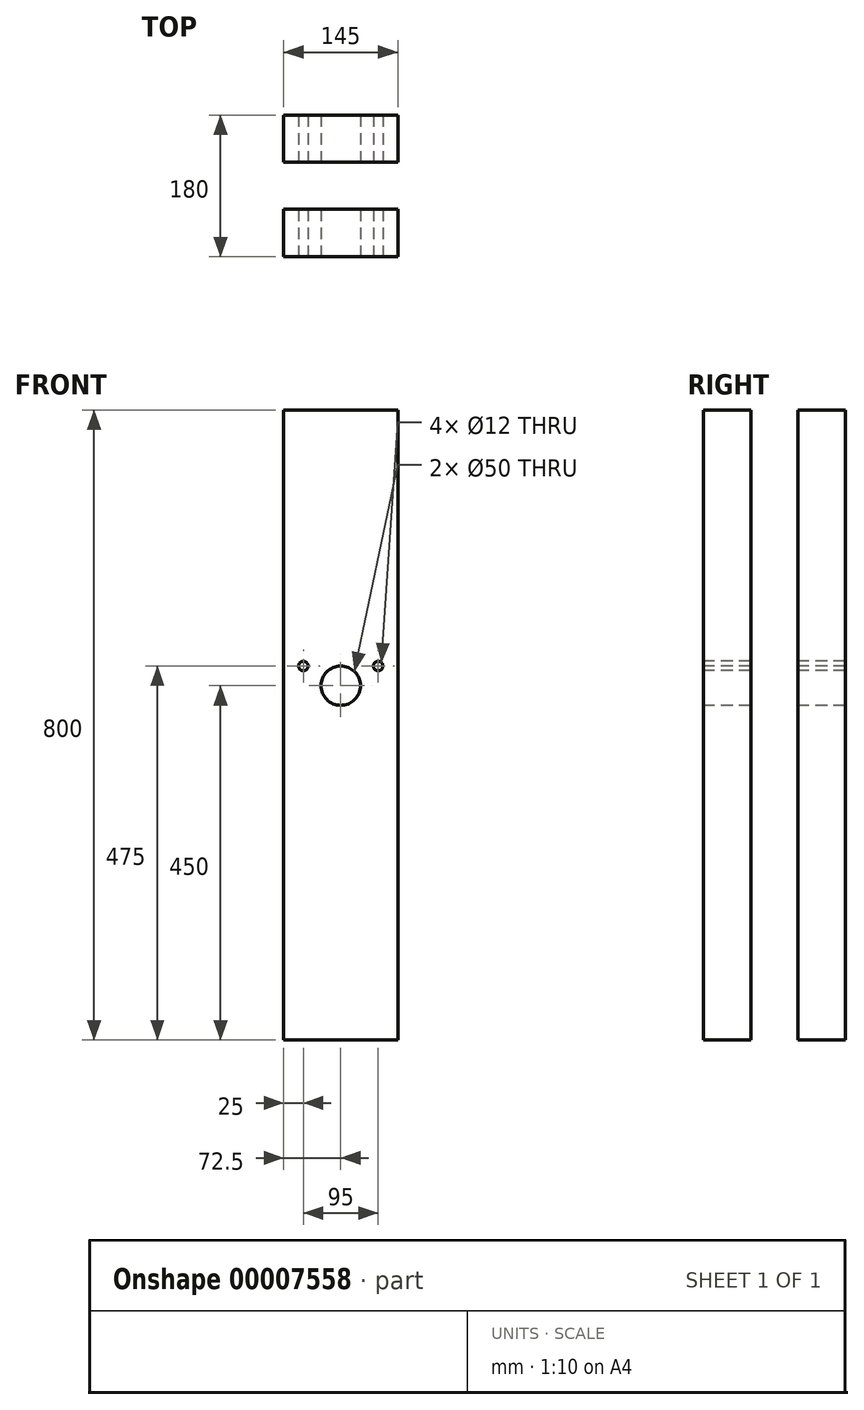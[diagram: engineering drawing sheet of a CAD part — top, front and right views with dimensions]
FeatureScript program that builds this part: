
annotation { "Feature Type Name" : "Feature", "Feature Type Description" : "" }
export const myFeature = defineFeature(function(context is Context, id is Id, definition is map)
    precondition{}
    {
        {
            var Q0;
            Q0=qCreatedBy(makeId("Top.planeOp"),FACE);
            var sketch = newSketch(context, id + "F0", { "sketchPlane" : qUnion([Q0])});
            skLineSegment(sketch, "E0.bottom", {"start": v(-72.5, -90) * mm, "end": v(72.5, -90) * mm});
            skLineSegment(sketch, "E0.top", {"start": v(-72.5, -30) * mm, "end": v(72.5, -30) * mm});
            skLineSegment(sketch, "E0.left", {"start": v(-72.5, -90) * mm, "end": v(-72.5, -30) * mm});
            skLineSegment(sketch, "E0.right", {"start": v(72.5, -90) * mm, "end": v(72.5, -30) * mm});
            skLineSegment(sketch, "E1.bottom", {"start": v(-72.5, 30) * mm, "end": v(72.5, 30) * mm});
            skLineSegment(sketch, "E1.top", {"start": v(-72.5, 90) * mm, "end": v(72.5, 90) * mm});
            skLineSegment(sketch, "E1.left", {"start": v(-72.5, 30) * mm, "end": v(-72.5, 90) * mm});
            skLineSegment(sketch, "E1.right", {"start": v(72.5, 30) * mm, "end": v(72.5, 90) * mm});
            skSolve(sketch);
        }
        {
            var Q0;
            Q0 = qSketchRegion(id + "F0", true);
            extrude(context, id + "F1", {"entities" : qUnion([Q0]), "endBound" : BoundingType.SYMMETRIC, "depth" : 800 * mm});
        }
        {
            var Q0;
            Q0=makeQuery(id+"F1.opExtrude","SWEPT_FACE",FACE,{"disambiguationData":[OSD([sQuery(id+"F0.wireOp",EDGE,"E0.bottom")])]});
            var sketch = newSketch(context, id + "F2", { "sketchPlane" : qUnion([Q0])});
            skCircle(sketch, "E2", {"center": v(0, 50) * mm, "radius": 25 * mm});
            skLineSegment(sketch, "E3", {"start": v(-72.5, 50) * mm, "end": v(72.5, 50) * mm, "construction": true});
            skCircle(sketch, "E4", {"center": v(-47.5, 75) * mm, "radius": 6 * mm});
            skCircle(sketch, "E5", {"center": v(47.5, 75) * mm, "radius": 6 * mm});
            skLineSegment(sketch, "E6", {"start": v(0, 132.46) * mm, "end": v(0, -49.39) * mm, "construction": true});
            skSolve(sketch);
        }
        {
            var Q0;
            Q0 = qSketchRegion(id + "F2", true);
            extrude(context, id + "F3", {"entities" : qUnion([Q0]), "operationType" : NewBodyOperationType.REMOVE, "endBound" : BoundingType.THROUGH_ALL, "oppositeDirection" : true, "depth" : 25 * mm});
        }
    });
